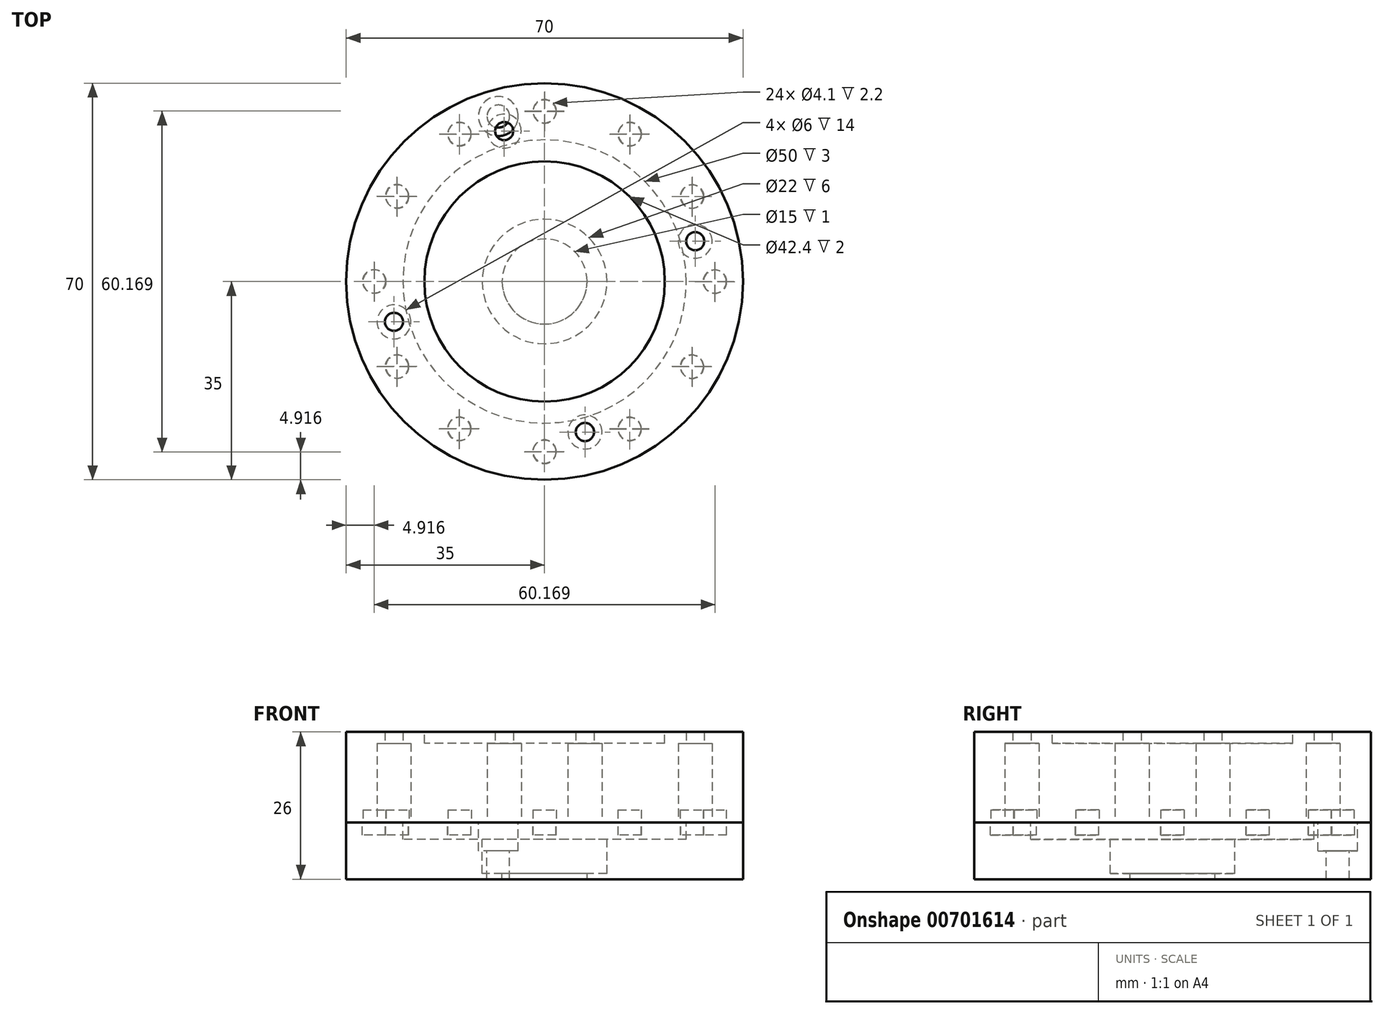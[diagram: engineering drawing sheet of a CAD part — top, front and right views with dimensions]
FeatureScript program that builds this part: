
annotation { "Feature Type Name" : "Feature", "Feature Type Description" : "" }
export const myFeature = defineFeature(function(context is Context, id is Id, definition is map)
    precondition{}
    {
        {
            var Q0;
            Q0=qCreatedBy(makeId("Top.planeOp"),FACE);
            var sketch = newSketch(context, id + "F0", { "sketchPlane" : qUnion([Q0])});
            skCircle(sketch, "E0", {"center": v(0, 0) * mm, "radius": 35 * mm});
            skSolve(sketch);
        }
        {
            var Q0;
            Q0 = qSketchRegion(id + "F0", true);
            extrude(context, id + "F1", {"entities" : qUnion([Q0]), "depth" : 16 * mm, "offsetDistance" : 25 * mm});
        }
        {
            var Q0;
            Q0=makeQuery(id+"F1.opExtrude","CAP_FACE",FACE,{"disambiguationData":[OSD([sQuery(id+"F0.wireOp",EDGE,"E0")])],"isStart":false});
            var sketch = newSketch(context, id + "F2", { "sketchPlane" : qUnion([Q0])});
            skCircle(sketch, "E1", {"center": v(0, 0) * mm, "radius": 21.2 * mm});
            skSolve(sketch);
        }
        {
            var Q0;
            Q0 = qSketchRegion(id + "F2", true);
            extrude(context, id + "F3", {"entities" : qUnion([Q0]), "operationType" : NewBodyOperationType.REMOVE, "oppositeDirection" : true, "depth" : 2 * mm, "offsetDistance" : 25 * mm});
        }
        {
            var Q0;
            Q0=makeQuery(id+"F1.opExtrude","CAP_FACE",FACE,{"disambiguationData":[OSD([sQuery(id+"F0.wireOp",EDGE,"E0")])],"isStart":true});
            var sketch = newSketch(context, id + "F4", { "sketchPlane" : qUnion([Q0])});
            skCircle(sketch, "E2", {"center": v(0, 30) * mm, "radius": 2.05 * mm});
            skCircle(sketch, "E3.1.0", {"center": v(-15, 25.98) * mm, "radius": 2.05 * mm});
            skCircle(sketch, "E3.2.0", {"center": v(-25.98, 15) * mm, "radius": 2.05 * mm});
            skCircle(sketch, "E3.3.0", {"center": v(-30, 0) * mm, "radius": 2.05 * mm});
            skCircle(sketch, "E3.4.0", {"center": v(-25.98, -15) * mm, "radius": 2.05 * mm});
            skCircle(sketch, "E3.5.0", {"center": v(-15, -25.98) * mm, "radius": 2.05 * mm});
            skCircle(sketch, "E3.6.0", {"center": v(0, -30) * mm, "radius": 2.05 * mm});
            skCircle(sketch, "E3.7.0", {"center": v(15, -25.98) * mm, "radius": 2.05 * mm});
            skCircle(sketch, "E3.8.0", {"center": v(25.98, -15) * mm, "radius": 2.05 * mm});
            skCircle(sketch, "E3.9.0", {"center": v(30, 0) * mm, "radius": 2.05 * mm});
            skCircle(sketch, "E3.10.0", {"center": v(25.98, 15) * mm, "radius": 2.05 * mm});
            skCircle(sketch, "E3.11.0", {"center": v(15, 25.98) * mm, "radius": 2.05 * mm});
            skPoint(sketch, "E3.center", {"position": v(0, 0) * mm});
            skSolve(sketch);
        }
        {
            var Q0;
            Q0 = qSketchRegion(id + "F4", true);
            extrude(context, id + "F5", {"entities" : qUnion([Q0]), "operationType" : NewBodyOperationType.REMOVE, "oppositeDirection" : true, "depth" : 2.2 * mm, "offsetDistance" : 25 * mm});
        }
        {
            var Q0;
            Q0=makeQuery(id+"F1.opExtrude","CAP_FACE",FACE,{"disambiguationData":[OSD([sQuery(id+"F0.wireOp",EDGE,"E0")])],"isStart":true});
            var sketch = newSketch(context, id + "F6", { "sketchPlane" : qUnion([Q0])});
            skLineSegment(sketch, "E4", {"start": v(0, 41.07) * mm, "end": v(0, -26.21) * mm, "construction": true});
            skLineSegment(sketch, "E5", {"start": v(32.7, 0) * mm, "end": v(-36.15, 0) * mm, "construction": true});
            skCircle(sketch, "E6", {"center": v(7.12, 26.56) * mm, "radius": 1.6 * mm});
            skCircle(sketch, "E7.1.0", {"center": v(-26.56, 7.12) * mm, "radius": 1.6 * mm});
            skCircle(sketch, "E7.2.0", {"center": v(-7.12, -26.56) * mm, "radius": 1.6 * mm});
            skCircle(sketch, "E7.3.0", {"center": v(26.56, -7.12) * mm, "radius": 1.6 * mm});
            skPoint(sketch, "E7.center", {"position": v(0, 0) * mm});
            skSolve(sketch);
        }
        {
            var Q0;
            Q0 = qSketchRegion(id + "F6", true);
            extrude(context, id + "F7", {"entities" : qUnion([Q0]), "operationType" : NewBodyOperationType.REMOVE, "endBound" : BoundingType.UP_TO_NEXT, "oppositeDirection" : true, "depth" : 25 * mm, "offsetDistance" : 25 * mm});
        }
        {
            var Q0;
            Q0=makeQuery(id+"F1.opExtrude","CAP_FACE",FACE,{"disambiguationData":[OSD([sQuery(id+"F0.wireOp",EDGE,"E0")])],"isStart":true});
            var sketch = newSketch(context, id + "F8", { "sketchPlane" : qUnion([Q0])});
            skCircle(sketch, "E8", {"center": v(7.12, 26.56) * mm, "radius": 3 * mm});
            skCircle(sketch, "E9.1.0", {"center": v(-26.56, 7.12) * mm, "radius": 3 * mm});
            skCircle(sketch, "E9.2.0", {"center": v(-7.12, -26.56) * mm, "radius": 3 * mm});
            skCircle(sketch, "E9.3.0", {"center": v(26.56, -7.12) * mm, "radius": 3 * mm});
            skPoint(sketch, "E9.center", {"position": v(0, 0) * mm});
            skSolve(sketch);
        }
        {
            var Q0;
            Q0 = qSketchRegion(id + "F8", true);
            extrude(context, id + "F9", {"entities" : qUnion([Q0]), "operationType" : NewBodyOperationType.REMOVE, "oppositeDirection" : true, "depth" : 14 * mm, "offsetDistance" : 25 * mm});
        }
        {
            var Q0;
            Q0=makeQuery(id+"F1.opExtrude","CAP_FACE",FACE,{"disambiguationData":[OSD([sQuery(id+"F0.wireOp",EDGE,"E0")])],"isStart":true});
            var sketch = newSketch(context, id + "F10", { "sketchPlane" : qUnion([Q0])});
            skCircle(sketch, "E10", {"center": v(0, 0) * mm, "radius": 35 * mm});
            skSolve(sketch);
        }
        {
            var Q0;
            Q0 = qSketchRegion(id + "F10", true);
            extrude(context, id + "F11", {"entities" : qUnion([Q0]), "depth" : 10 * mm, "offsetDistance" : 25 * mm});
        }
        {
            var Q0;
            Q0=makeQuery(id+"F11.opExtrude","CAP_FACE",FACE,{"disambiguationData":[OSD([sQuery(id+"F10.wireOp",EDGE,"E10")])],"isStart":true});
            var sketch = newSketch(context, id + "F12", { "sketchPlane" : qUnion([Q0])});
            skCircle(sketch, "E11.0.0", {"center": v(0, 0) * mm, "radius": 35 * mm});
            skCircle(sketch, "E12", {"center": v(0.03, 30.08) * mm, "radius": 2.05 * mm});
            skCircle(sketch, "E13.1.0", {"center": v(-15.02, 26.07) * mm, "radius": 2.05 * mm});
            skCircle(sketch, "E13.2.0", {"center": v(-26.04, 15.06) * mm, "radius": 2.05 * mm});
            skCircle(sketch, "E13.3.0", {"center": v(-30.08, 0.03) * mm, "radius": 2.05 * mm});
            skCircle(sketch, "E13.4.0", {"center": v(-26.07, -15.02) * mm, "radius": 2.05 * mm});
            skCircle(sketch, "E13.5.0", {"center": v(-15.06, -26.04) * mm, "radius": 2.05 * mm});
            skCircle(sketch, "E13.6.0", {"center": v(-0.03, -30.08) * mm, "radius": 2.05 * mm});
            skCircle(sketch, "E13.7.0", {"center": v(15.02, -26.07) * mm, "radius": 2.05 * mm});
            skCircle(sketch, "E13.8.0", {"center": v(26.04, -15.06) * mm, "radius": 2.05 * mm});
            skCircle(sketch, "E13.9.0", {"center": v(30.08, -0.03) * mm, "radius": 2.05 * mm});
            skCircle(sketch, "E13.10.0", {"center": v(26.07, 15.02) * mm, "radius": 2.05 * mm});
            skCircle(sketch, "E13.11.0", {"center": v(15.06, 26.04) * mm, "radius": 2.05 * mm});
            skSolve(sketch);
        }
        {
            var Q0;
            Q0=makeQuery(id+"F12.imprint","IMPRINT",FACE,{"disambiguationData":[TD([[makeQuery(id+"F12.imprint","IMPRINT",EDGE,{"derivedFrom":sQuery(id+"F12.wireOp",EDGE,"E13.3.0")}),1.0]])]});
            var Q1;
            Q1=makeQuery(id+"F12.imprint","IMPRINT",FACE,{"disambiguationData":[TD([[makeQuery(id+"F12.imprint","IMPRINT",EDGE,{"derivedFrom":sQuery(id+"F12.wireOp",EDGE,"E13.11.0")}),1.0]])]});
            var Q2;
            Q2=makeQuery(id+"F12.imprint","IMPRINT",FACE,{"disambiguationData":[TD([[makeQuery(id+"F12.imprint","IMPRINT",EDGE,{"derivedFrom":sQuery(id+"F12.wireOp",EDGE,"E13.10.0")}),1.0]])]});
            var Q3;
            Q3=makeQuery(id+"F12.imprint","IMPRINT",FACE,{"disambiguationData":[TD([[makeQuery(id+"F12.imprint","IMPRINT",EDGE,{"derivedFrom":sQuery(id+"F12.wireOp",EDGE,"E13.9.0")}),1.0]])]});
            var Q4;
            Q4=makeQuery(id+"F12.imprint","IMPRINT",FACE,{"disambiguationData":[TD([[makeQuery(id+"F12.imprint","IMPRINT",EDGE,{"derivedFrom":sQuery(id+"F12.wireOp",EDGE,"E13.8.0")}),1.0]])]});
            var Q5;
            Q5=makeQuery(id+"F12.imprint","IMPRINT",FACE,{"disambiguationData":[TD([[makeQuery(id+"F12.imprint","IMPRINT",EDGE,{"derivedFrom":sQuery(id+"F12.wireOp",EDGE,"E13.7.0")}),1.0]])]});
            var Q6;
            Q6=makeQuery(id+"F12.imprint","IMPRINT",FACE,{"disambiguationData":[TD([[makeQuery(id+"F12.imprint","IMPRINT",EDGE,{"derivedFrom":sQuery(id+"F12.wireOp",EDGE,"E13.6.0")}),1.0]])]});
            var Q7;
            Q7=makeQuery(id+"F12.imprint","IMPRINT",FACE,{"disambiguationData":[TD([[makeQuery(id+"F12.imprint","IMPRINT",EDGE,{"derivedFrom":sQuery(id+"F12.wireOp",EDGE,"E13.5.0")}),1.0]])]});
            var Q8;
            Q8=makeQuery(id+"F12.imprint","IMPRINT",FACE,{"disambiguationData":[TD([[makeQuery(id+"F12.imprint","IMPRINT",EDGE,{"derivedFrom":sQuery(id+"F12.wireOp",EDGE,"E13.4.0")}),1.0]])]});
            var Q9;
            Q9=makeQuery(id+"F12.imprint","IMPRINT",FACE,{"disambiguationData":[TD([[makeQuery(id+"F12.imprint","IMPRINT",EDGE,{"derivedFrom":sQuery(id+"F12.wireOp",EDGE,"E13.2.0")}),1.0]])]});
            var Q10;
            Q10=makeQuery(id+"F12.imprint","IMPRINT",FACE,{"disambiguationData":[TD([[makeQuery(id+"F12.imprint","IMPRINT",EDGE,{"derivedFrom":sQuery(id+"F12.wireOp",EDGE,"E13.1.0")}),1.0]])]});
            var Q11;
            Q11=makeQuery(id+"F12.imprint","IMPRINT",FACE,{"disambiguationData":[TD([[makeQuery(id+"F12.imprint","IMPRINT",EDGE,{"derivedFrom":sQuery(id+"F12.wireOp",EDGE,"E12")}),1.0]])]});
            extrude(context, id + "F13", {"entities" : qUnion([Q0, Q1, Q2, Q3, Q4, Q5, Q6, Q7, Q8, Q9, Q10, Q11]), "operationType" : NewBodyOperationType.REMOVE, "oppositeDirection" : true, "depth" : 2.2 * mm, "offsetDistance" : 25 * mm});
        }
        {
            var Q0;
            Q0=makeQuery(id+"F11.opExtrude","CAP_FACE",FACE,{"disambiguationData":[OSD([sQuery(id+"F10.wireOp",EDGE,"E10")])],"isStart":true});
            var sketch = newSketch(context, id + "F14", { "sketchPlane" : qUnion([Q0])});
            skCircle(sketch, "E14", {"center": v(0, 0) * mm, "radius": 25 * mm});
            skSolve(sketch);
        }
        {
            var Q0;
            Q0 = qSketchRegion(id + "F14", true);
            extrude(context, id + "F15", {"entities" : qUnion([Q0]), "operationType" : NewBodyOperationType.REMOVE, "oppositeDirection" : true, "depth" : 3 * mm, "offsetDistance" : 25 * mm});
        }
        {
            var Q0;
            Q0=makeQuery(id+"F15.boolean.opBoolean","COPY",FACE,{"derivedFrom":makeQuery(id+"F15.opExtrude","CAP_FACE",FACE,{"disambiguationData":[OSD([sQuery(id+"F14.wireOp",EDGE,"E14")])],"isStart":false})});
            var sketch = newSketch(context, id + "F16", { "sketchPlane" : qUnion([Q0])});
            skCircle(sketch, "E15", {"center": v(0, 0) * mm, "radius": 11 * mm});
            skSolve(sketch);
        }
        {
            var Q0;
            Q0 = qSketchRegion(id + "F16", true);
            extrude(context, id + "F17", {"entities" : qUnion([Q0]), "operationType" : NewBodyOperationType.REMOVE, "oppositeDirection" : true, "depth" : 6 * mm, "offsetDistance" : 25 * mm});
        }
        {
            var Q0;
            Q0=makeQuery(id+"F11.opExtrude","CAP_FACE",FACE,{"disambiguationData":[OSD([sQuery(id+"F10.wireOp",EDGE,"E10")])],"isStart":true});
            var sketch = newSketch(context, id + "F18", { "sketchPlane" : qUnion([Q0])});
            skCircle(sketch, "E16", {"center": v(-8.16, 29.17) * mm, "radius": 3.5 * mm});
            skSolve(sketch);
        }
        {
            var Q0;
            Q0 = qSketchRegion(id + "F18", true);
            extrude(context, id + "F19", {"entities" : qUnion([Q0]), "operationType" : NewBodyOperationType.REMOVE, "oppositeDirection" : true, "depth" : 5 * mm, "offsetDistance" : 25 * mm});
        }
        {
            var Q0;
            Q0=makeQuery(id+"F19.boolean.opBoolean","COPY",FACE,{"derivedFrom":makeQuery(id+"F19.opExtrude","CAP_FACE",FACE,{"disambiguationData":[OSD([sQuery(id+"F18.wireOp",EDGE,"E16")])],"isStart":false})});
            var sketch = newSketch(context, id + "F20", { "sketchPlane" : qUnion([Q0])});
            skCircle(sketch, "E17", {"center": v(-8.16, 29.17) * mm, "radius": 2 * mm});
            skSolve(sketch);
        }
        {
            var Q0;
            Q0 = qSketchRegion(id + "F20", true);
            extrude(context, id + "F21", {"entities" : qUnion([Q0]), "operationType" : NewBodyOperationType.REMOVE, "endBound" : BoundingType.UP_TO_NEXT, "oppositeDirection" : true, "depth" : 25 * mm, "offsetDistance" : 25 * mm});
        }
        {
            var Q0;
            Q0=makeQuery(id+"F17.boolean.opBoolean","COPY",FACE,{"derivedFrom":makeQuery(id+"F17.opExtrude","CAP_FACE",FACE,{"disambiguationData":[OSD([sQuery(id+"F16.wireOp",EDGE,"E15")])],"isStart":false})});
            var sketch = newSketch(context, id + "F22", { "sketchPlane" : qUnion([Q0])});
            skCircle(sketch, "E18", {"center": v(0, 0) * mm, "radius": 7.5 * mm});
            skSolve(sketch);
        }
        {
            var Q0;
            Q0 = qSketchRegion(id + "F22", true);
            extrude(context, id + "F23", {"entities" : qUnion([Q0]), "operationType" : NewBodyOperationType.REMOVE, "endBound" : BoundingType.UP_TO_NEXT, "oppositeDirection" : true, "depth" : 25 * mm, "offsetDistance" : 25 * mm});
        }
    });
